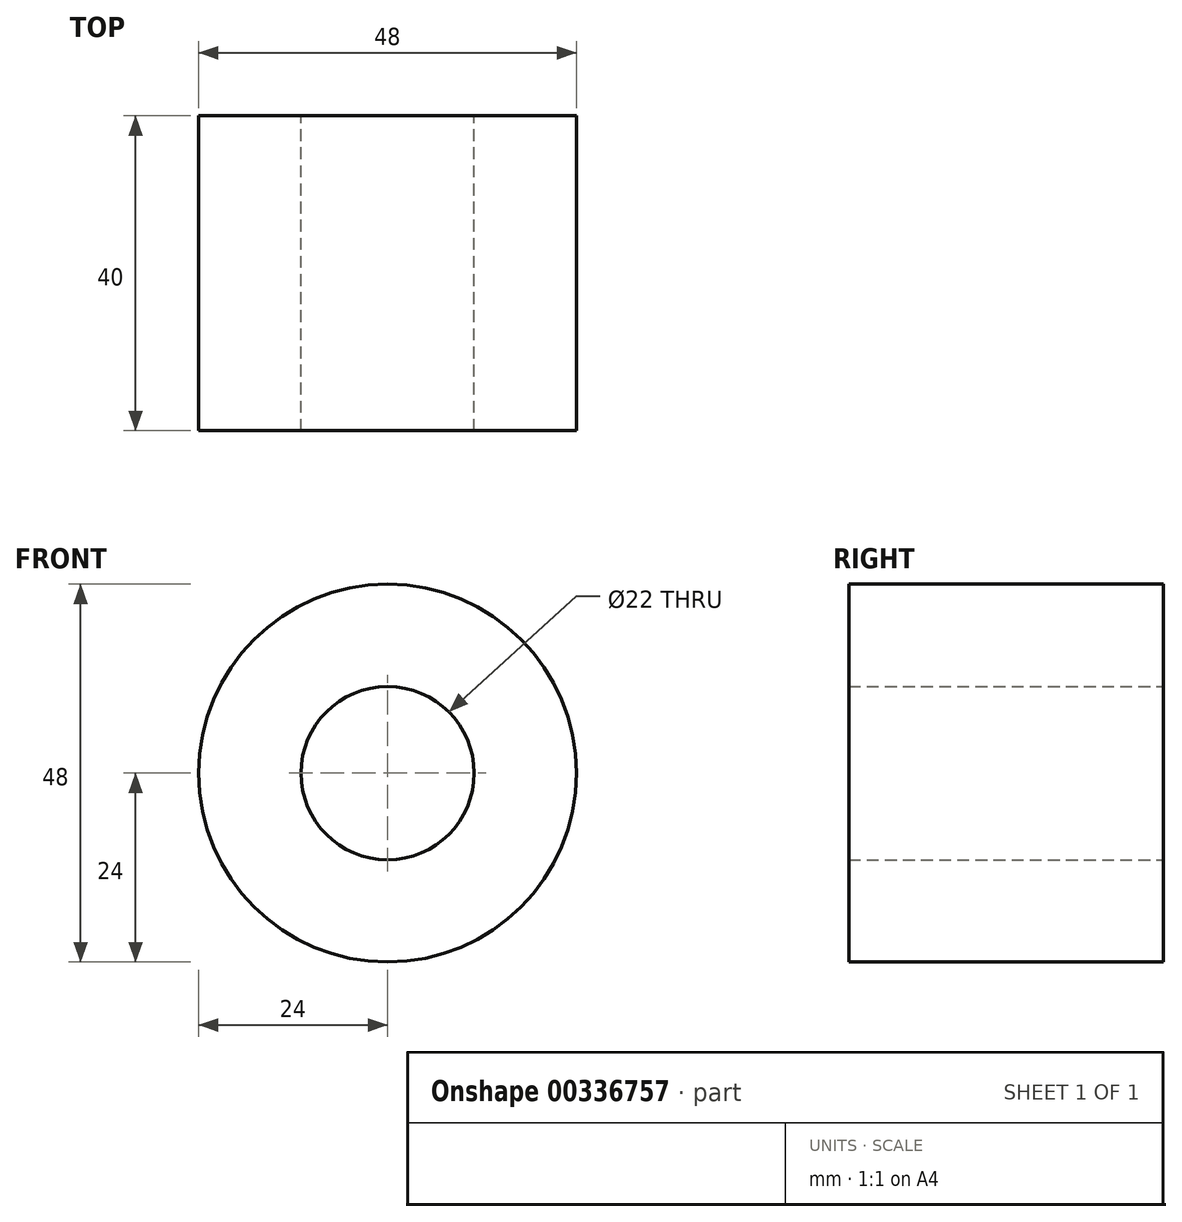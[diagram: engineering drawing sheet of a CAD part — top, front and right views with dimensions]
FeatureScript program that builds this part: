
annotation { "Feature Type Name" : "Feature", "Feature Type Description" : "" }
export const myFeature = defineFeature(function(context is Context, id is Id, definition is map)
    precondition{}
    {
        {
            var Q0;
            Q0=qCreatedBy(makeId("Front.planeOp"),FACE);
            var sketch = newSketch(context, id + "F0", { "sketchPlane" : qUnion([Q0])});
            skCircle(sketch, "E0", {"center": v(0, 0) * mm, "radius": 11 * mm});
            skCircle(sketch, "E1", {"center": v(0, 0) * mm, "radius": 24 * mm});
            skSolve(sketch);
        }
        {
            var Q0;
            Q0=makeQuery(id+"F0.imprint","IMPRINT",FACE,{"disambiguationData":[TD([[makeQuery(id+"F0.imprint","IMPRINT",EDGE,{"derivedFrom":sQuery(id+"F0.wireOp",EDGE,"E0")}),-1.0]])]});
            extrude(context, id + "F1", {"entities" : qUnion([Q0]), "depth" : 12 * mm});
        }
        {
            var Q0;
            Q0=makeQuery(id+"F1.opExtrude","CAP_FACE",FACE,{"disambiguationData":[OSD([sQuery(id+"F0.wireOp",EDGE,"E0"),sQuery(id+"F0.wireOp",EDGE,"E1")])],"isStart":false});
            var sketch = newSketch(context, id + "F2", { "sketchPlane" : qUnion([Q0])});
            skCircle(sketch, "E2", {"center": v(0, 0) * mm, "radius": 11 * mm});
            skCircle(sketch, "E3", {"center": v(0, 0) * mm, "radius": 24 * mm});
            skSolve(sketch);
        }
        {
            var Q0;
            Q0=makeQuery(id+"F2.imprint","IMPRINT",FACE,{"disambiguationData":[TD([[makeQuery(id+"F2.imprint","IMPRINT",EDGE,{"derivedFrom":sQuery(id+"F2.wireOp",EDGE,"E2")}),-1.0]])]});
            extrude(context, id + "F3", {"entities" : qUnion([Q0]), "operationType" : NewBodyOperationType.ADD, "depth" : 16 * mm});
        }
        {
            var Q0;
            Q0=makeQuery(id+"F3.opExtrude","CAP_FACE",FACE,{"disambiguationData":[OSD([sQuery(id+"F2.wireOp",EDGE,"E2"),sQuery(id+"F2.wireOp",EDGE,"E3")])],"isStart":false});
            var sketch = newSketch(context, id + "F4", { "sketchPlane" : qUnion([Q0])});
            skCircle(sketch, "E4", {"center": v(0, 0) * mm, "radius": 24 * mm});
            skCircle(sketch, "E5", {"center": v(0, 0) * mm, "radius": 11 * mm});
            skSolve(sketch);
        }
        {
            var Q0;
            Q0=makeQuery(id+"F4.imprint","IMPRINT",FACE,{"disambiguationData":[TD([[makeQuery(id+"F4.imprint","IMPRINT",EDGE,{"derivedFrom":sQuery(id+"F4.wireOp",EDGE,"E4")}),1.0]])]});
            extrude(context, id + "F5", {"entities" : qUnion([Q0]), "operationType" : NewBodyOperationType.ADD, "depth" : 12 * mm});
        }
    });
